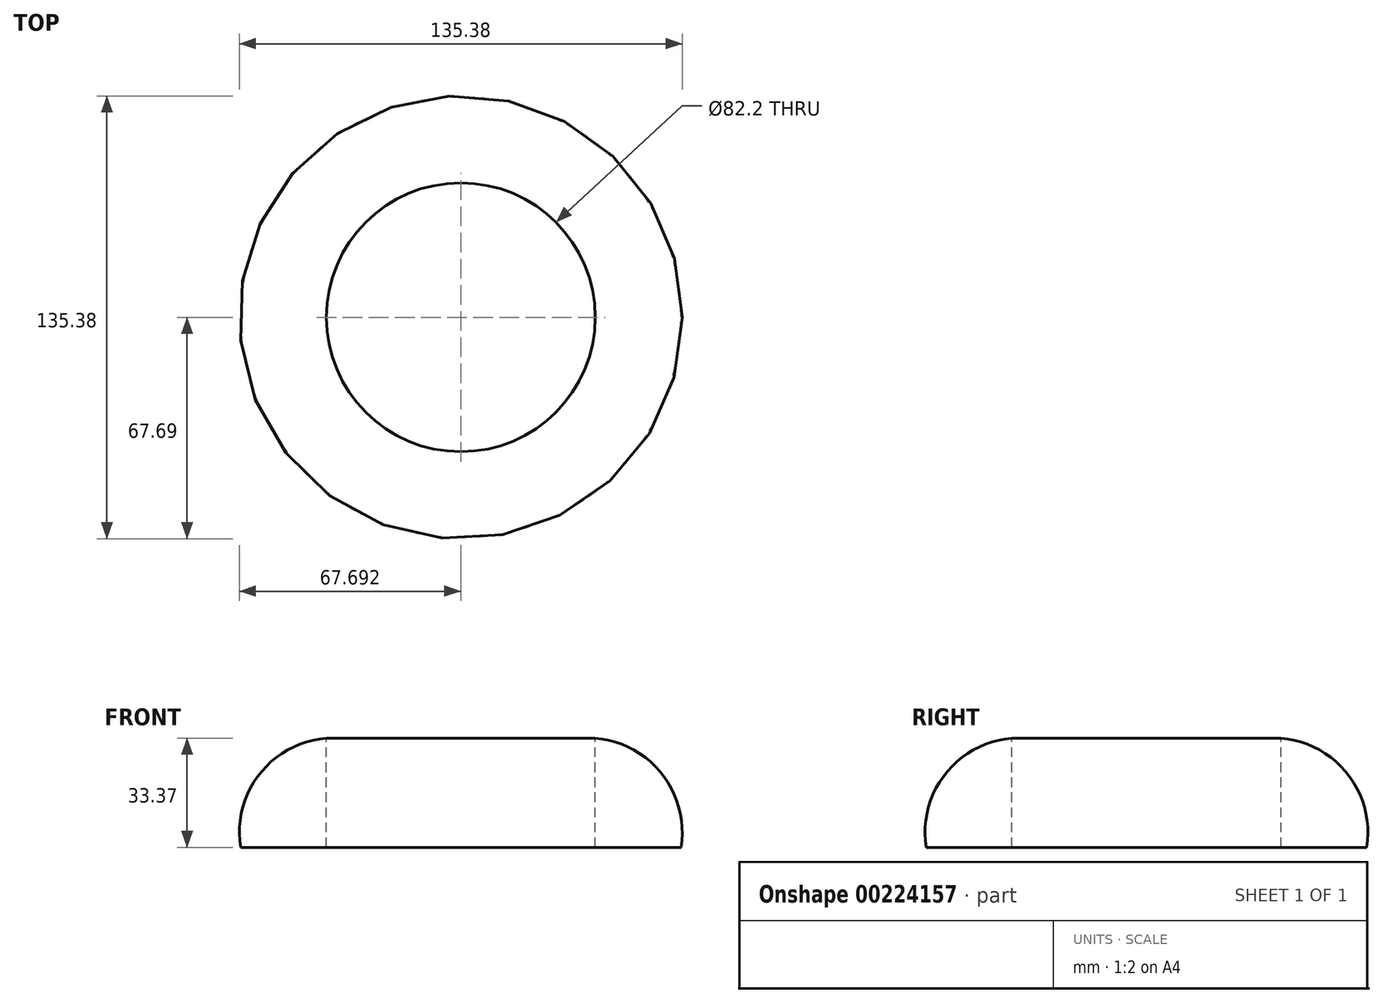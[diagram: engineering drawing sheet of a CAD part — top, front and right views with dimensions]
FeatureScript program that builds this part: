
annotation { "Feature Type Name" : "Feature", "Feature Type Description" : "" }
export const myFeature = defineFeature(function(context is Context, id is Id, definition is map)
    precondition{}
    {
        {
            var Q0;
            Q0=qCreatedBy(makeId("Front.planeOp"),FACE);
            var sketch = newSketch(context, id + "F0", { "sketchPlane" : qUnion([Q0])});
            skArc(sketch, "E0", {"start": v(26.23, 0) * mm, "mid": v(20.41, 22.42) * mm, "end": v(0, 33.37) * mm});
            skLineSegment(sketch, "E1", {"start": v(0, 33.37) * mm, "end": v(0, 0) * mm});
            skLineSegment(sketch, "E2", {"start": v(26.23, 0) * mm, "end": v(0, 0) * mm});
            skLineSegment(sketch, "E3", {"start": v(-41.1, 33.37) * mm, "end": v(-41.1, -28.42) * mm});
            skSolve(sketch);
        }
        {
            var Q0;
            Q0=makeQuery(id+"F0.imprint","IMPRINT",FACE,{"disambiguationData":[TD([[makeQuery(id+"F0.imprint","IMPRINT",EDGE,{"derivedFrom":sQuery(id+"F0.wireOp",EDGE,"E0")}),1.0]])]});
            var Q1;
            Q1=sQuery(id+"F0.wireOp",EDGE,"E3");
            revolve(context, id + "F1", {"entities" : qUnion([Q0]), "axis" : qUnion([Q1]), "revolveType" : RevolveType.FULL});
        }
    });
